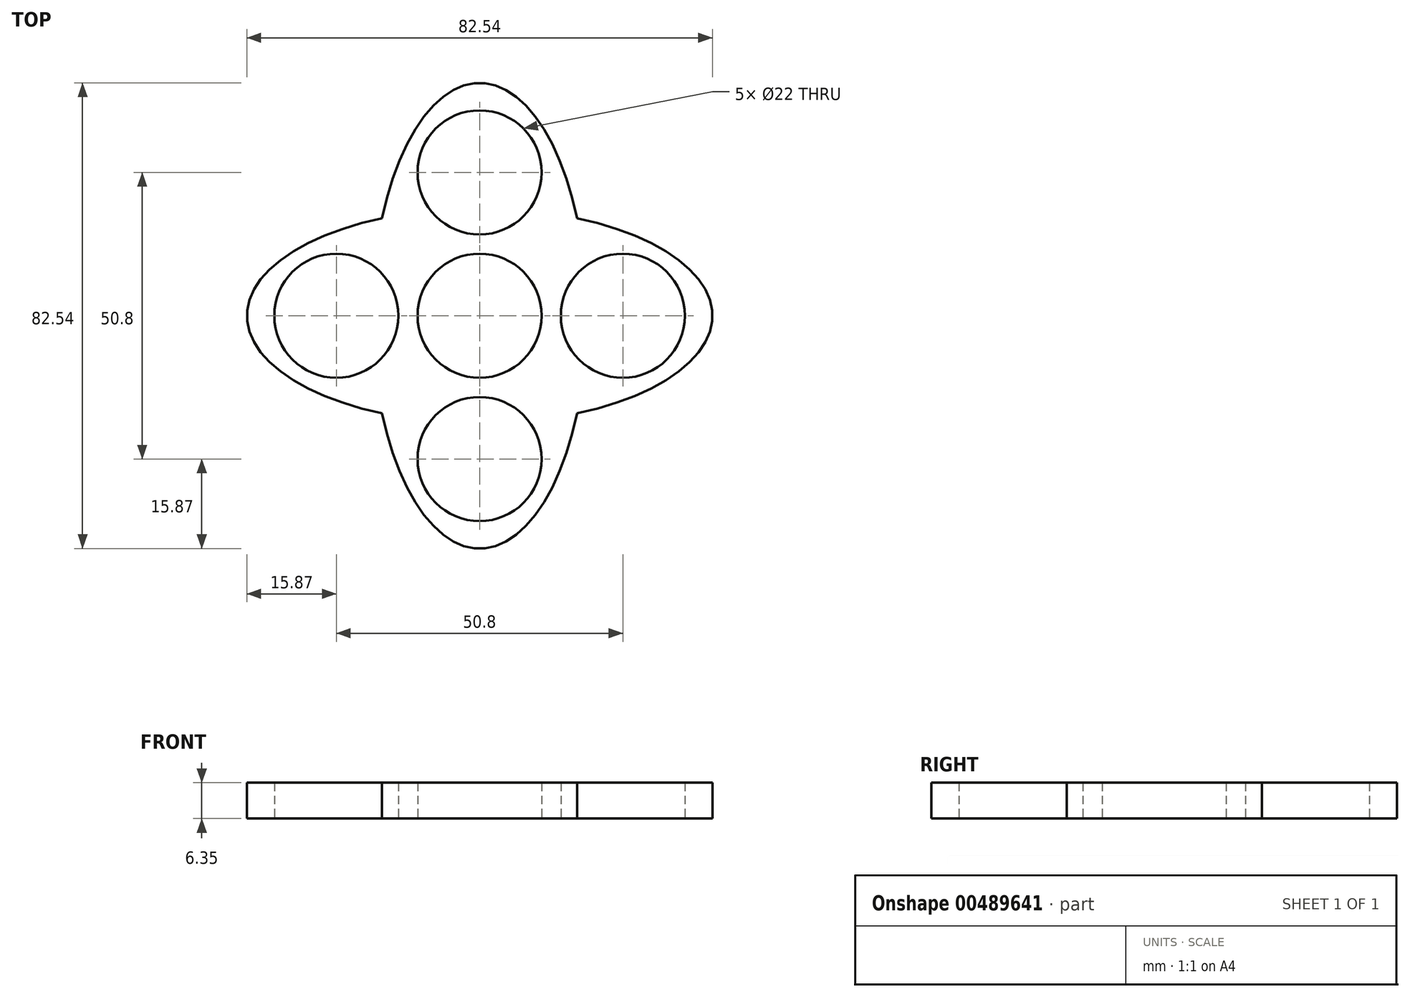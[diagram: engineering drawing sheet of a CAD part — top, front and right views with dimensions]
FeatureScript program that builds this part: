
annotation { "Feature Type Name" : "Feature", "Feature Type Description" : "" }
export const myFeature = defineFeature(function(context is Context, id is Id, definition is map)
    precondition{}
    {
        {
            var Q0;
            Q0=qCreatedBy(makeId("Top.planeOp"),FACE);
            var sketch = newSketch(context, id + "F0", { "sketchPlane" : qUnion([Q0])});
            skCircle(sketch, "E0", {"center": v(0, 0) * mm, "radius": 11 * mm});
            skEllipse(sketch, "E1", {"center": v(0, 0) * mm, "majorRadius": 41.28 * mm, "minorRadius": 19.05 * mm, "majorAxis": v(1, 0)});
            skEllipse(sketch, "E2", {"center": v(0, 0) * mm, "majorRadius": 41.28 * mm, "minorRadius": 19.05 * mm, "majorAxis": v(0, 1)});
            skCircle(sketch, "E3", {"center": v(0, 25.4) * mm, "radius": 11 * mm});
            skCircle(sketch, "E4.1.0", {"center": v(-25.4, 0) * mm, "radius": 11 * mm});
            skCircle(sketch, "E4.2.0", {"center": v(0, -25.4) * mm, "radius": 11 * mm});
            skCircle(sketch, "E4.3.0", {"center": v(25.4, 0) * mm, "radius": 11 * mm});
            skSolve(sketch);
        }
        {
            var Q0;
            Q0 = qSketchRegion(id + "F0", true);
            extrude(context, id + "F1", {"entities" : qUnion([Q0]), "depth" : 25.4 * mm});
        }
        {
            var Q0;
            Q0=makeQuery(id+"F1.opExtrude","CAP_FACE",FACE,{"disambiguationData":[OSD([sQuery(id+"F0.wireOp",EDGE,"E0"),sQuery(id+"F0.wireOp",EDGE,"E1"),sQuery(id+"F0.wireOp",EDGE,"E2"),sQuery(id+"F0.wireOp",EDGE,"E3"),sQuery(id+"F0.wireOp",EDGE,"E4.1.0"),sQuery(id+"F0.wireOp",EDGE,"E4.2.0"),sQuery(id+"F0.wireOp",EDGE,"E4.3.0")])],"isStart":false});
            extrude(context, id + "F2", {"entities" : qUnion([Q0]), "operationType" : NewBodyOperationType.REMOVE, "oppositeDirection" : true, "depth" : 19.05 * mm});
        }
    });
